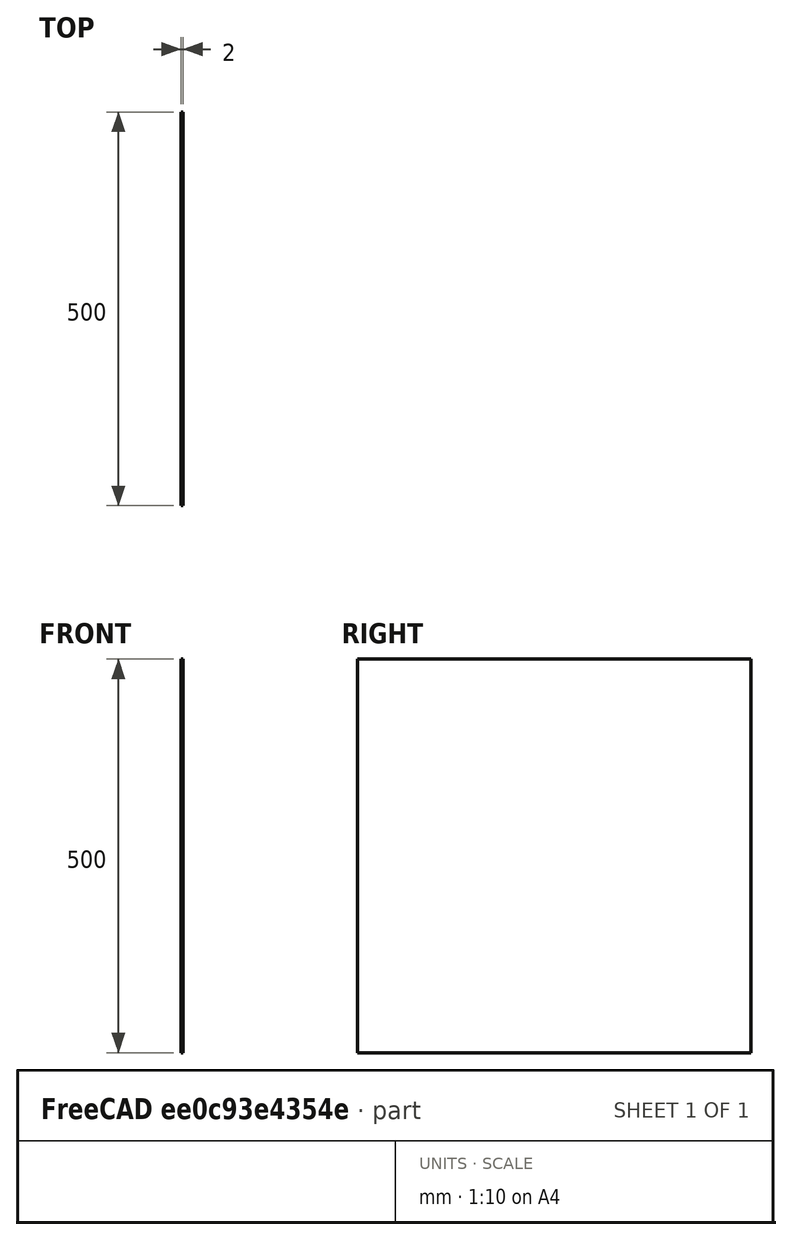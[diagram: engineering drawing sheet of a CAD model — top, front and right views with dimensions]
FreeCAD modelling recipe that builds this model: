
FCSTD DOCUMENT  (FreeCAD 0.19R24276 (Git))
Label: 4000_Body_Window_500x500x2_YZ
License: All rights reserved
LicenseURL: http://en.wikipedia.org/wiki/All_rights_reserved
objects: Sketcher::SketchObject×1, Spreadsheet::Sheet×1, PartDesign::Pad×1, PartDesign::Body×1
note: 4 computed .brp shape members not serialized (recipe doc carries the construction recipe); baked Part::Feature solids carry a one-line shape summary decoded from their .brp

FEATURE [Sketcher::SketchObject] Sketch
  FullyConstrained = true
  MapMode = 4
  Placement = pos=(0,0,0) rot=(0.57735,0.57735,0.57735;2.0944rad)
  Support = -> [XY_Plane]
  expr: Constraints[5] = Spreadsheet.nZ
  expr: Constraints[6] = Spreadsheet.nY
  sketch-geometry (5):
    g0: LineSegment StartX=0 StartY=0 StartZ=0 EndX=0 EndY=500 EndZ=0
    g1: LineSegment StartX=500 StartY=0 StartZ=0 EndX=500 EndY=500 EndZ=0
    g2: LineSegment StartX=500 StartY=500 StartZ=0 EndX=0 EndY=500 EndZ=0
    g3: LineSegment StartX=250 StartY=0 StartZ=0 EndX=0 EndY=0 EndZ=0
    g4: LineSegment StartX=500 StartY=0 StartZ=0 EndX=250 EndY=0 EndZ=0
  constraints (14):
    c: Vertical(g0)
    c: Vertical(g1)
    c: Coincident(g2,g1)
    c: Coincident(g2,g0)
    c: Horizontal(g2)
    c: DistanceY(g1,g1) = 500
    c: DistanceX(g2,g2) = 500
    c: Coincident(g3,g0)
    c: Coincident(g4,g1)
    c: Horizontal(g4)
    c: Equal(g3,g4)
    c: Coincident(g4,g3)
    c: Horizontal(g3)
    c: Coincident(g0,g-1)
FEATURE [Spreadsheet::Sheet] Spreadsheet  label="xls"
  cells = B7=KEYBOARD FRONT; B8=Width; C8=nY; D8(nY)=500; B9=Height; C9=nZ; D9(nZ)=500; E9=F(T); B10=Thickness; C10=nT; D10(nT)=2
FEATURE [PartDesign::Pad] Pad
  AllowMultiFace = false
  Direction = (1,1,1)
  Length = 2
  Length2 = 100
  Profile = -> Sketch
  Reversed = true
  Type = 0
  expr: Length = Spreadsheet.nT
FEATURE [PartDesign::Body] Body
  Group = -> [Sketch,Pad]
  Origin = -> Origin
  Tip = -> Pad
